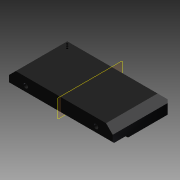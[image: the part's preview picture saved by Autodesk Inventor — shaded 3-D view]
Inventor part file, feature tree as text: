
AUTODESK INVENTOR PART (.ipt)
format: ipt  version: 2015 (Build 190159000, 159)  size: 373,760 bytes
history: native  units: mm
features: extrude x13, reference x8, fillet x4, chamfer x3, hole x3
ambient origin geometry x8: Origin, YZ Plane, XZ Plane, XY Plane, X Axis, Y Axis, Z Axis, Center Point
bodies: Solid1 (feature_tree)
feature tree (31):
  extrude  "Extrusión1"  Depth=155.0mm
  chamfer  "Chaflán11"  Distance=83.0mm
  extrude  "Extrusión39"  Depth=5.0mm
  hole  "Agujero6"  [1 undecoded]
  extrude  "Extrusión49"  Depth=50.0mm
  extrude  "Extrusión50"  Depth=5.0mm
  extrude  "Extrusión51"  Depth=25.0mm TaperAngle=0.0deg
  extrude  "Extrusión55"  Depth=15.0mm
  extrude  "Extrusión56"  Depth=10.0mm
  chamfer  "Chaflán16"  Distance=5.0mm
  chamfer  "Chaflán17"  Distance=5.0mm
  hole  "Agujero10"  [1 undecoded]
  hole  "Agujero11"  [1 undecoded]
  extrude  "Extrusión57"  Depth=3.5mm TaperAngle=0.0deg
  extrude  "Extrusión58"  Depth=105.0mm
  fillet  "Empalme39"  Radius=13.3mm
  fillet  "Empalme40"  [1 undecoded]
  extrude  "Extrusión59"  Depth=4.0mm
  extrude  "Extrusión60"  Depth=9.0mm
  extrude  "Extrusión61"  Depth=4.0mm
  fillet  "Empalme41"  Radius=7.0mm
  fillet  "Empalme42"  Radius=2.5mm
  extrude  "Extrusión62"  Depth=3.0mm
  reference  "Referencia11"
  reference  "Referencia12"
  reference  "Referencia13"
  reference  "Referencia14"
  reference  "Referencia15"
  reference  "Referencia16"
  reference  "Referencia17"
  reference  "Referencia18"
note: 4 required parameter values undecoded (feature->parameter linkage not recoverable at this tier; creation-order binding heuristic only, values carry confidence <= 0.55)
